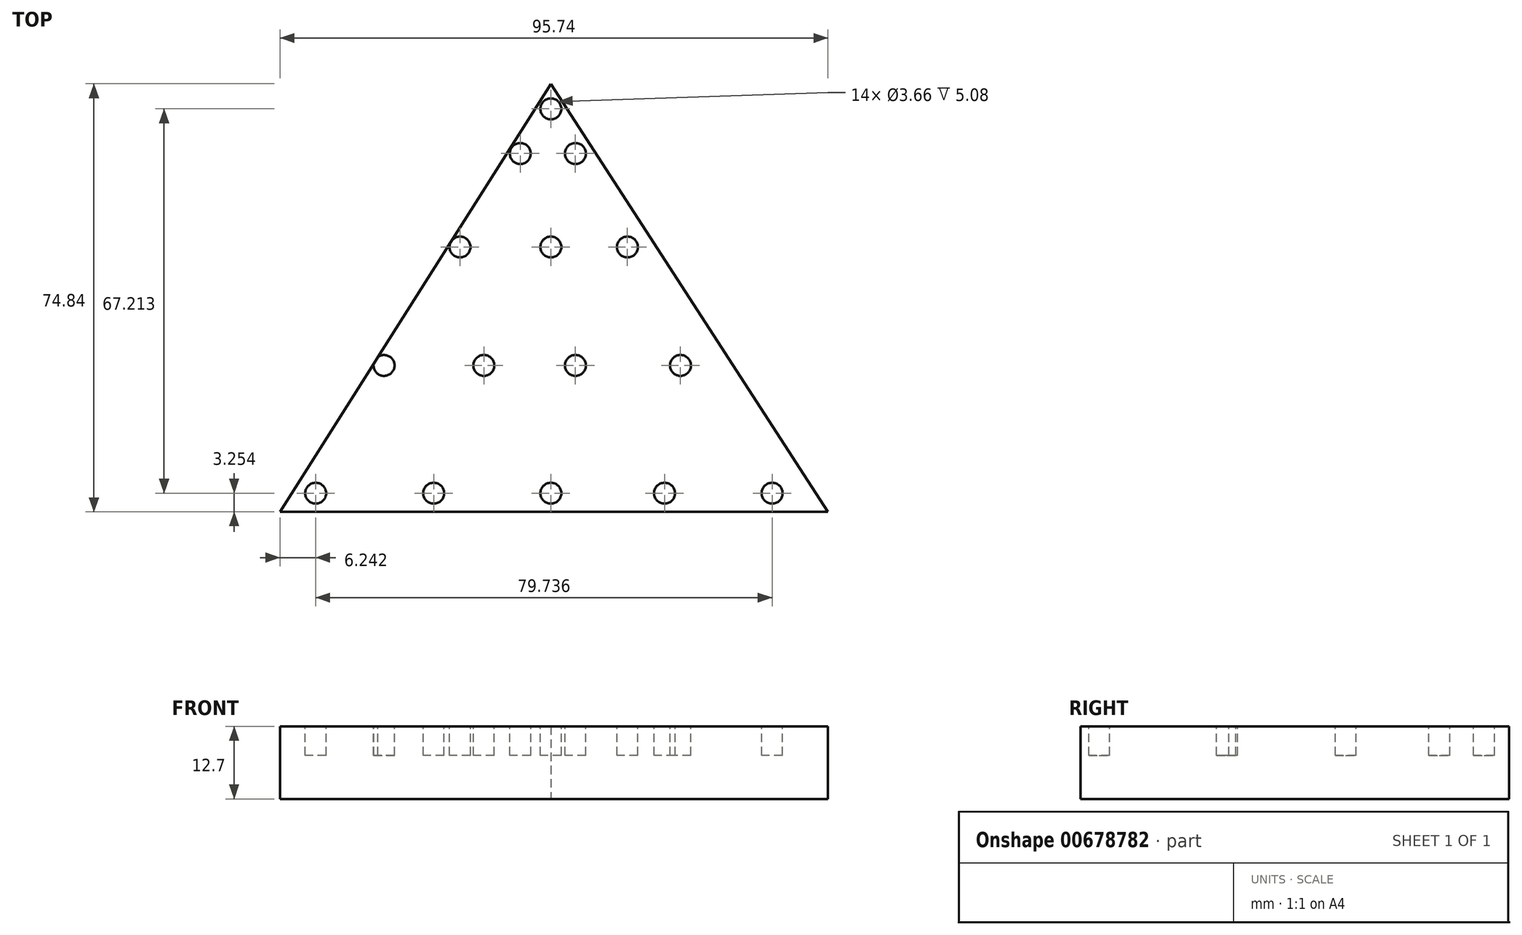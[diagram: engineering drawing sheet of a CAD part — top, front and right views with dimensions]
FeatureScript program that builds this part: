
annotation { "Feature Type Name" : "Feature", "Feature Type Description" : "" }
export const myFeature = defineFeature(function(context is Context, id is Id, definition is map)
    precondition{}
    {
        {
            var Q0;
            Q0=qCreatedBy(makeId("Top.planeOp"),FACE);
            var sketch = newSketch(context, id + "F0", { "sketchPlane" : qUnion([Q0])});
            skLineSegment(sketch, "E0", {"start": v(0, 52.6) * mm, "end": v(-47.32, -22.23) * mm});
            skLineSegment(sketch, "E1", {"start": v(-47.32, -22.23) * mm, "end": v(48.42, -22.23) * mm});
            skLineSegment(sketch, "E2", {"start": v(48.42, -22.23) * mm, "end": v(0, 52.6) * mm});
            skSolve(sketch);
        }
        {
            var Q0;
            Q0=makeQuery(id+"F0.imprint","IMPRINT",FACE,{"disambiguationData":[TD([[makeQuery(id+"F0.imprint","IMPRINT",EDGE,{"derivedFrom":sQuery(id+"F0.wireOp",EDGE,"E0")}),1.0]])]});
            extrude(context, id + "F1", {"entities" : qUnion([Q0]), "depth" : 12.7 * mm, "offsetDistance" : 25.4 * mm});
        }
        {
            var Q0;
            Q0=makeQuery(id+"F1.opExtrude","CAP_FACE",FACE,{"disambiguationData":[OSD([sQuery(id+"F0.wireOp",EDGE,"E0"),sQuery(id+"F0.wireOp",EDGE,"E1"),sQuery(id+"F0.wireOp",EDGE,"E2")])],"isStart":false});
            var sketch = newSketch(context, id + "F2", { "sketchPlane" : qUnion([Q0])});
            skCircle(sketch, "E3", {"center": v(-41.08, -18.98) * mm, "radius": 1.83 * mm});
            skCircle(sketch, "E4", {"center": v(-20.46, -18.98) * mm, "radius": 1.83 * mm});
            skCircle(sketch, "E5", {"center": v(0, -18.98) * mm, "radius": 1.83 * mm});
            skCircle(sketch, "E6", {"center": v(19.86, -18.98) * mm, "radius": 1.83 * mm});
            skCircle(sketch, "E7", {"center": v(38.66, -18.98) * mm, "radius": 1.83 * mm});
            skCircle(sketch, "E8", {"center": v(-29.14, 3.36) * mm, "radius": 1.83 * mm});
            skCircle(sketch, "E9", {"center": v(-11.7, 3.36) * mm, "radius": 1.83 * mm});
            skCircle(sketch, "E10", {"center": v(4.3, 3.36) * mm, "radius": 1.83 * mm});
            skCircle(sketch, "E11", {"center": v(22.64, 3.36) * mm, "radius": 1.83 * mm});
            skCircle(sketch, "E12", {"center": v(-15.87, 24.07) * mm, "radius": 1.83 * mm});
            skCircle(sketch, "E13", {"center": v(0, 24.07) * mm, "radius": 1.83 * mm});
            skCircle(sketch, "E14", {"center": v(13.38, 24.07) * mm, "radius": 1.83 * mm});
            skCircle(sketch, "E15", {"center": v(-5.34, 40.43) * mm, "radius": 1.83 * mm});
            skCircle(sketch, "E16", {"center": v(4.3, 40.43) * mm, "radius": 1.83 * mm});
            skCircle(sketch, "E17", {"center": v(0, 48.24) * mm, "radius": 1.83 * mm});
            skSolve(sketch);
        }
        {
            var Q0;
            Q0 = qSketchRegion(id + "F2", true);
            extrude(context, id + "F3", {"entities" : qUnion([Q0]), "operationType" : NewBodyOperationType.REMOVE, "oppositeDirection" : true, "depth" : 5.08 * mm, "offsetDistance" : 25.4 * mm});
        }
        {
            var Q0;
            Q0=qCreatedBy(makeId("Top.planeOp"),FACE);
            var sketch = newSketch(context, id + "F4", { "sketchPlane" : qUnion([Q0])});
            skCircle(sketch, "E18", {"center": v(-65.96, 44.16) * mm, "radius": 1.45 * mm});
            skSolve(sketch);
        }
        {
            var Q0;
            Q0=sQuery(id+"F4.wireOp",EDGE,"E18");
            extrude(context, id + "F5", {"bodyType" : ToolBodyType.SURFACE, "surfaceEntities" : qUnion([Q0]), "depth" : 25.4 * mm, "offsetDistance" : 25.4 * mm});
        }
    });
